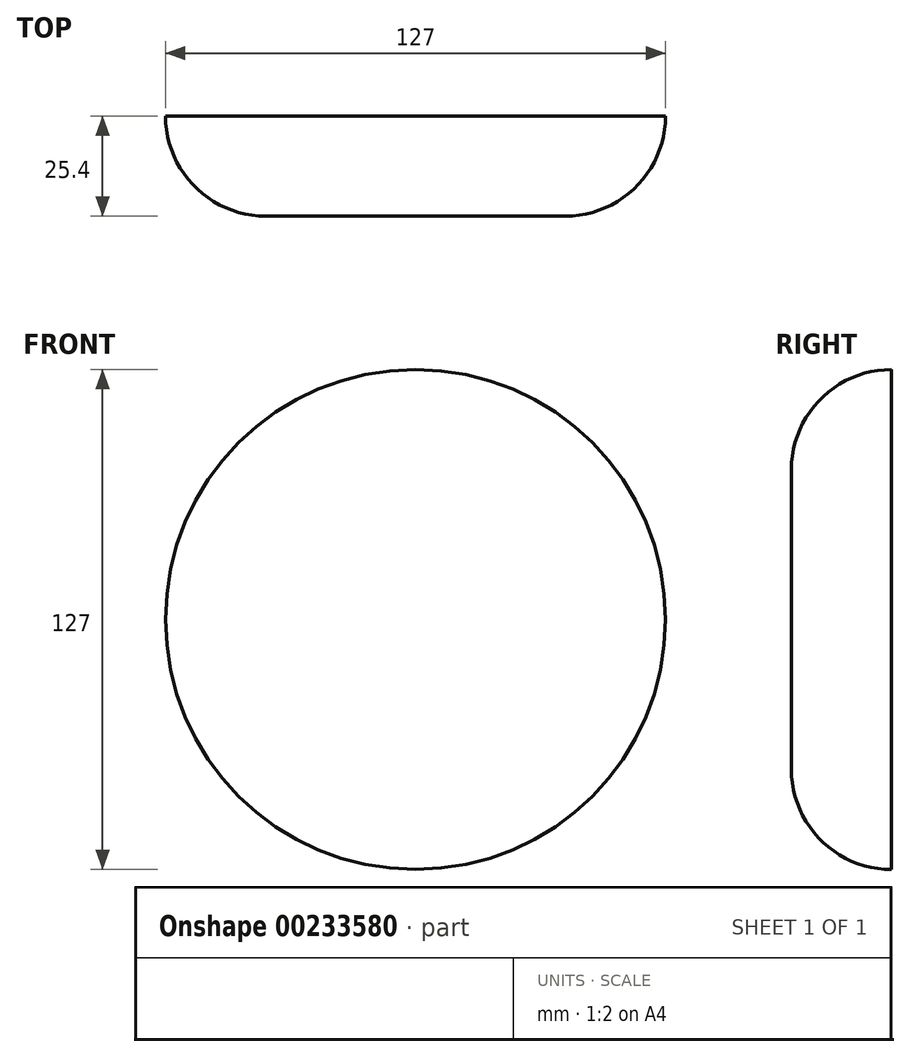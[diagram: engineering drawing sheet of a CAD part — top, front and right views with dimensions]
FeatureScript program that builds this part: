
annotation { "Feature Type Name" : "Feature", "Feature Type Description" : "" }
export const myFeature = defineFeature(function(context is Context, id is Id, definition is map)
    precondition{}
    {
        {
            var Q0;
            Q0=qCreatedBy(makeId("Front.planeOp"),FACE);
            var sketch = newSketch(context, id + "F0", { "sketchPlane" : qUnion([Q0])});
            skCircle(sketch, "E0", {"center": v(0, 0) * mm, "radius": 63.5 * mm});
            skSolve(sketch);
        }
        {
            var Q0;
            Q0=qSketchRegion(id+"F0",true);
            extrude(context, id + "F1", {"entities" : qUnion([Q0]), "depth" : 25.4 * mm});
        }
        {
            var Q0;
            Q0=makeQuery(id+"F1.opExtrude","CAP_EDGE",EDGE,{"disambiguationData":[OSD([sQuery(id+"F0.wireOp",EDGE,"E0")])],"isStart":false});
            fillet(context, id + "F2", {"entities" : qUnion([Q0]), "radius" : 25.4 * mm, "tangentPropagation" : true, "allowEdgeOverflow" : false});
        }
    });
